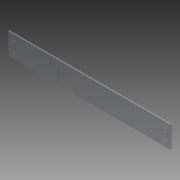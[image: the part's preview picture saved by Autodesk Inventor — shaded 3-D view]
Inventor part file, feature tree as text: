
AUTODESK INVENTOR PART (.ipt)
format: ipt  version: 2014 (Build 180170000, 170)  size: 93,696 bytes
history: native  units: in
note: dims shown in document units (in); Inventor stores cm internally (conversion verified against a paired STEP export)
features: extrude x2, sketch x2
ambient origin geometry x8: Origin, YZ Plane, XZ Plane, XY Plane, X Axis, Y Axis, Z Axis, Center Point
bodies: Solid1 (feature_tree)
feature tree (4):
  extrude  "Extrusion1"  Depth=15.0in
  extrude  "Extrusion2"  Depth=4.5in
  sketch  "Sketch1"  dims[d0=2.0in d1=15.0in]
  sketch  "Sketch2"  dims[d2=0.163in d3=0.5in d4=0.5in d5=0.7874in d7=1.0in d8=0.7874in d10=14.0in d13=0.125in d14=0.0in d15=1.25in d16=1.5in d17=4.5in d18=1.0in d19=0.0in]
